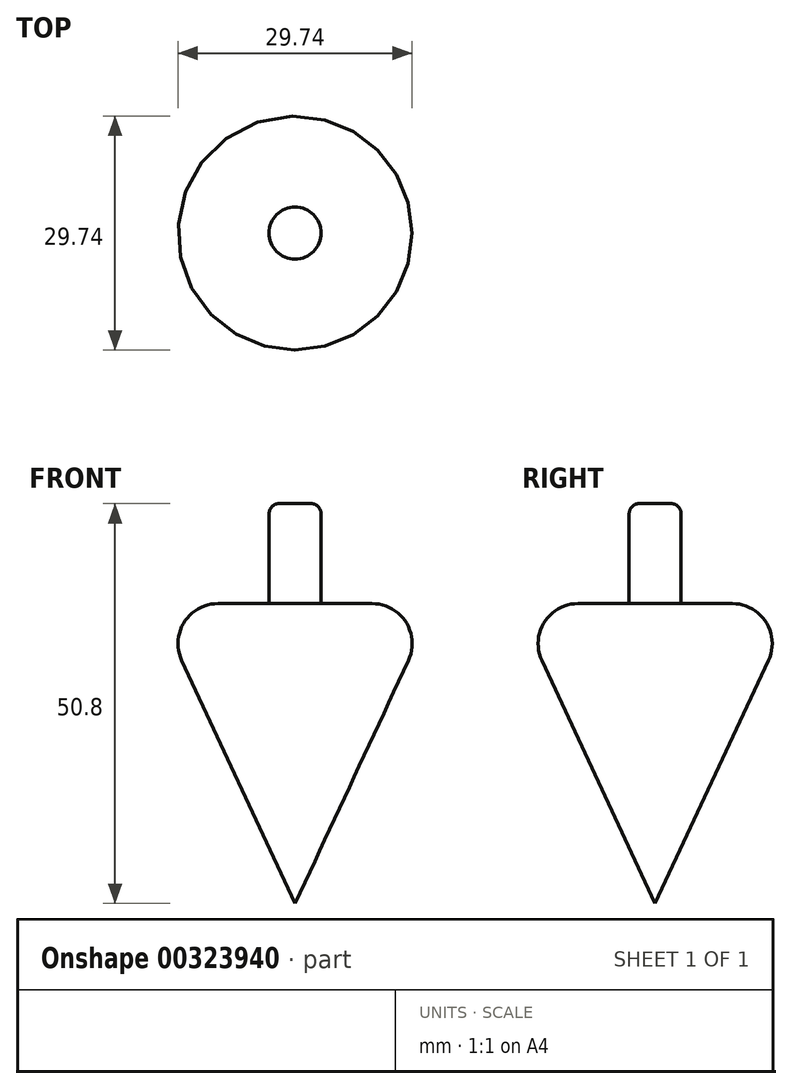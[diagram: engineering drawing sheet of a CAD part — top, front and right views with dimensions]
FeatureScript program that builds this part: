
annotation { "Feature Type Name" : "Feature", "Feature Type Description" : "" }
export const myFeature = defineFeature(function(context is Context, id is Id, definition is map)
    precondition{}
    {
        {
            var Q0;
            Q0=qCreatedBy(makeId("Front.planeOp"),FACE);
            var sketch = newSketch(context, id + "F0", { "sketchPlane" : qUnion([Q0])});
            skLineSegment(sketch, "E0", {"start": v(0, 36) * mm, "end": v(0, -73.55) * mm, "construction": true});
            skLineSegment(sketch, "E1", {"start": v(-51.1, 0) * mm, "end": v(76.87, 0) * mm, "construction": true});
            skLineSegment(sketch, "E2", {"start": v(-17.77, 0) * mm, "end": v(0, -38.1) * mm});
            skLineSegment(sketch, "E3", {"start": v(0, -38.1) * mm, "end": v(17.77, 0) * mm});
            skLineSegment(sketch, "E4", {"start": v(17.77, 0) * mm, "end": v(-17.77, 0) * mm});
            skLineSegment(sketch, "E5", {"start": v(-3.3, 0) * mm, "end": v(-3.3, 12.7) * mm});
            skLineSegment(sketch, "E6", {"start": v(-3.3, 12.7) * mm, "end": v(0, 12.7) * mm});
            skLineSegment(sketch, "E7.MirrorCS", {"start": v(3.3, 0) * mm, "end": v(3.3, 12.7) * mm});
            skLineSegment(sketch, "E8.MirrorCS", {"start": v(3.3, 12.7) * mm, "end": v(0, 12.7) * mm});
            skLineSegment(sketch, "E9", {"start": v(-17.77, 0) * mm, "end": v(17.77, 0) * mm});
            skLineSegment(sketch, "E10", {"start": v(0, 0) * mm, "end": v(0, -38.1) * mm});
            skLineSegment(sketch, "E11", {"start": v(0, 12.7) * mm, "end": v(0, 0) * mm});
            skSolve(sketch);
        }
        {
            var Q0;
            {var subQ0=sQuery(id+"F0.wireOp",EDGE,"E2");Q0=makeQuery(id+"F0.imprint","IMPRINT",FACE,{"disambiguationData":[TD([[makeQuery(id+"F0.imprint","IMPRINT",EDGE,{"derivedFrom":subQ0}),1.0]])]});}
            var Q1;
            {var subQ0=sQuery(id+"F0.wireOp",EDGE,"E5");Q1=makeQuery(id+"F0.imprint","IMPRINT",FACE,{"disambiguationData":[TD([[makeQuery(id+"F0.imprint","IMPRINT",EDGE,{"derivedFrom":subQ0}),-1.0]])]});}
            var Q2;
            Q2=sQuery(id+"F0.wireOp",EDGE,"E10");
            revolve(context, id + "F1", {"entities" : qUnion([Q0, Q1]), "axis" : qUnion([Q2]), "revolveType" : RevolveType.FULL});
        }
        {
            var Q0;
            Q0=makeQuery(id+"F1.opRevolve","SWEPT_EDGE",EDGE,{"disambiguationData":[OSD([sQuery(id+"F0.wireOp",EDGE,"E2"),sQuery(id+"F0.wireOp",EDGE,"E9")])]});
            fillet(context, id + "F2", {"entities" : qUnion([Q0]), "radius" : 5.08 * mm, "tangentPropagation" : true, "allowEdgeOverflow" : false});
        }
        {
            var Q0;
            Q0=makeQuery(id+"F1.opRevolve","SWEPT_EDGE",EDGE,{"disambiguationData":[OSD([sQuery(id+"F0.wireOp",EDGE,"E5"),sQuery(id+"F0.wireOp",EDGE,"E6")])]});
            fillet(context, id + "F3", {"entities" : qUnion([Q0]), "radius" : 1.27 * mm, "tangentPropagation" : true, "allowEdgeOverflow" : false});
        }
    });
